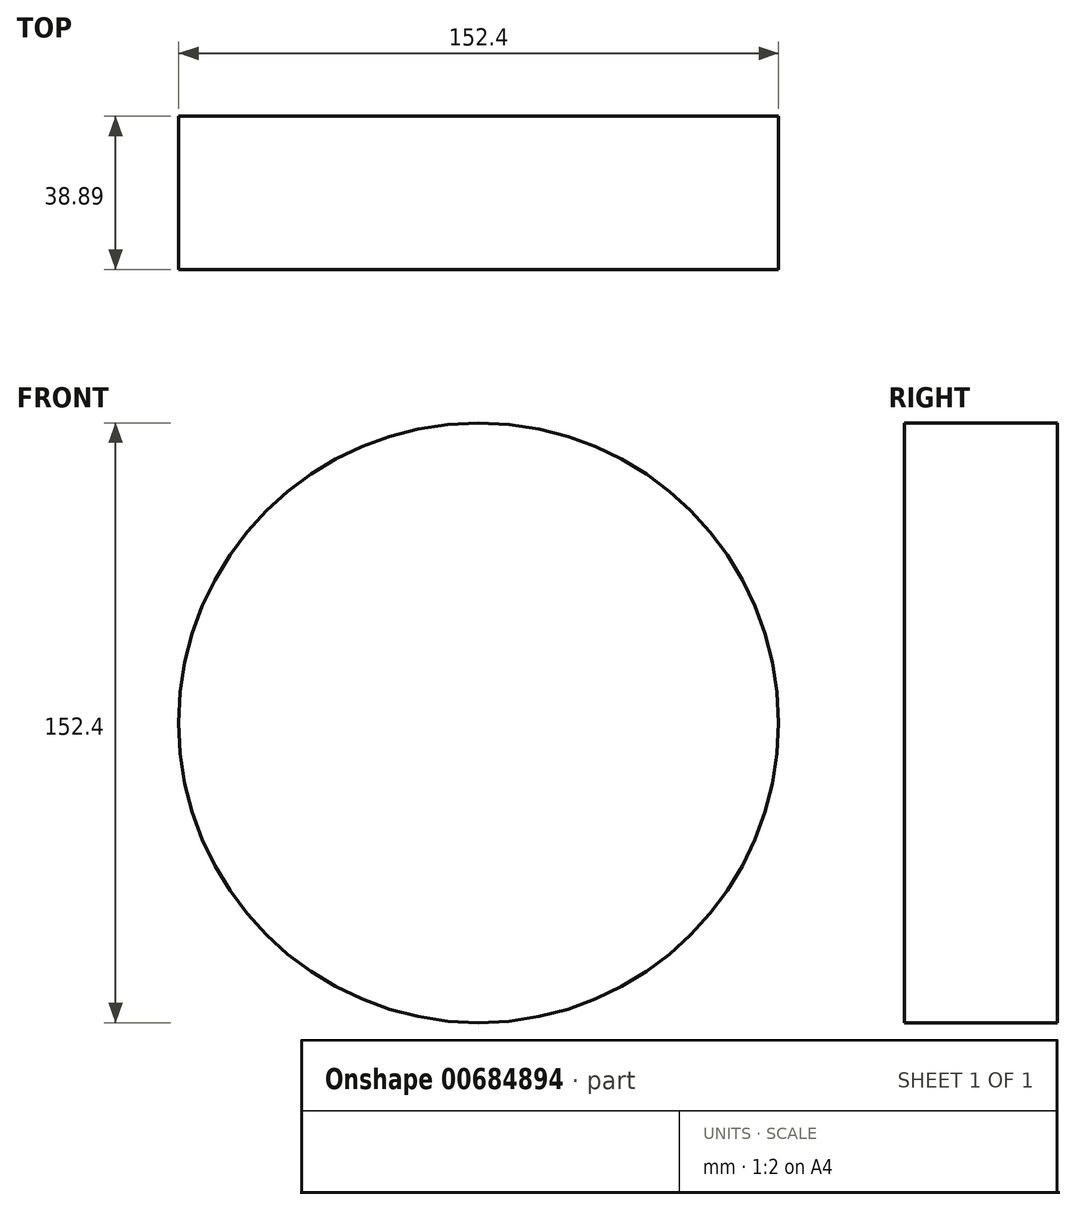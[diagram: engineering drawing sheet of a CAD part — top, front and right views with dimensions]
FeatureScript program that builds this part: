
annotation { "Feature Type Name" : "Feature", "Feature Type Description" : "" }
export const myFeature = defineFeature(function(context is Context, id is Id, definition is map)
    precondition{}
    {
        {
            var Q0;
            Q0=qCreatedBy(makeId("Front.planeOp"),FACE);
            var sketch = newSketch(context, id + "F0", { "sketchPlane" : qUnion([Q0])});
            skCircle(sketch, "E0", {"center": v(0, 0) * mm, "radius": 76.2 * mm});
            skSolve(sketch);
        }
        {
            var Q0;
            Q0 = qSketchRegion(id + "F0", true);
            extrude(context, id + "F1", {"entities" : qUnion([Q0]), "depth" : 38.9 * mm, "offsetDistance" : 25.4 * mm});
        }
    });
